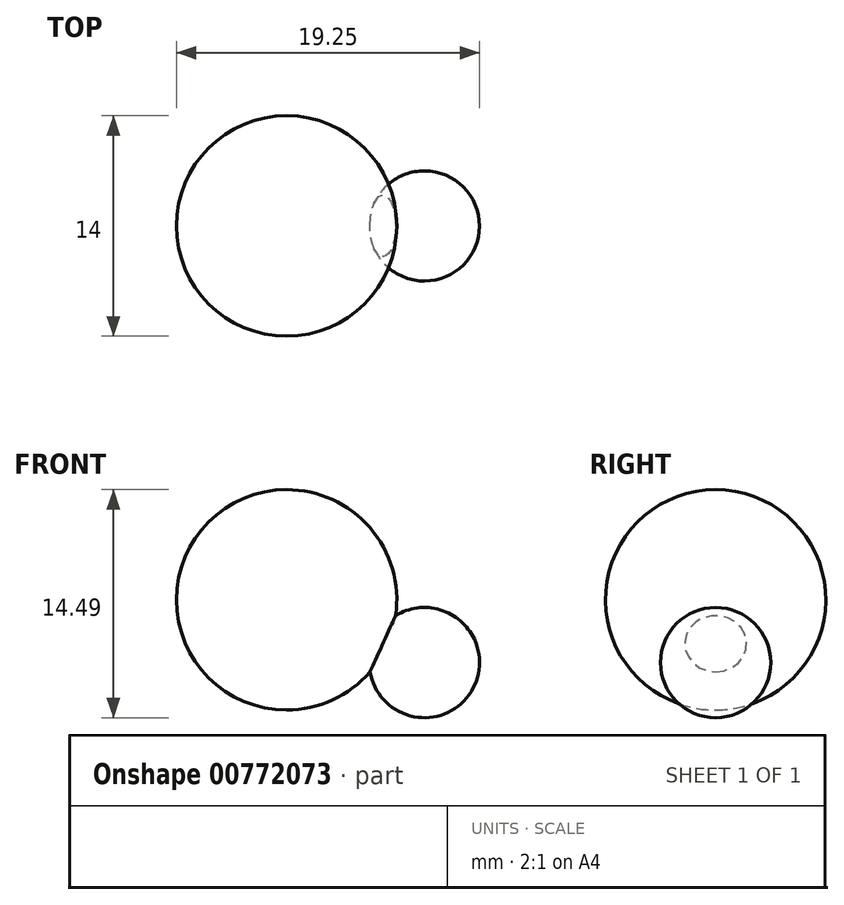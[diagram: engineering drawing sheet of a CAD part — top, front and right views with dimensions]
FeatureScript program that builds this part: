
annotation { "Feature Type Name" : "Feature", "Feature Type Description" : "" }
export const myFeature = defineFeature(function(context is Context, id is Id, definition is map)
    precondition{}
    {
        {
            var Q0;
            Q0=qCreatedBy(makeId("Front.planeOp"),FACE);
            var sketch = newSketch(context, id + "F0", { "sketchPlane" : qUnion([Q0])});
            skLineSegment(sketch, "E0", {"start": v(0, 0) * mm, "end": v(0, 14) * mm});
            skArc(sketch, "E1", {"start": v(0, 0) * mm, "mid": v(7, 7) * mm, "end": v(0, 14) * mm});
            skSolve(sketch);
        }
        {
            var Q0;
            Q0=qCreatedBy(makeId("Front.planeOp"),FACE);
            var sketch = newSketch(context, id + "F1", { "sketchPlane" : qUnion([Q0])});
            skLineSegment(sketch, "E2", {"start": v(0, 0) * mm, "end": v(0, 13.87) * mm, "construction": true});
            skLineSegment(sketch, "E3", {"start": v(0, 6.93) * mm, "end": v(6.62, 9.21) * mm, "construction": true});
            skSolve(sketch);
        }
        {
            var Q0;
            Q0=sQuery(id+"F1.wireOp",VERTEX,"E3.end");
            var Q1;
            Q1=sQuery(id+"F1.wireOp",EDGE,"E3");
            cPlane(context, id + "F2", {"entities" : qUnion([Q0, Q1]), "cplaneType" : CPlaneType.LINE_POINT, "offset" : 25.4 * mm, "width" : 152.4 * mm, "height" : 152.4 * mm});
        }
        {
            var Q0;
            Q0=makeQuery(id+"F0.imprint","IMPRINT",FACE,{"disambiguationData":[TD([[makeQuery(id+"F0.imprint","IMPRINT",EDGE,{"derivedFrom":sQuery(id+"F0.wireOp",EDGE,"E0")}),-1.0]])]});
            var Q1;
            Q1=sQuery(id+"F0.wireOp",EDGE,"E0");
            revolve(context, id + "F3", {"surfaceOperationType" : NewSurfaceOperationType.NEW, "entities" : qUnion([Q0]), "axis" : qUnion([Q1]), "revolveType" : RevolveType.FULL});
        }
        {
            var Q0;
            Q0=qCreatedBy(id+"F2.planeOp",FACE);
            var sketch = newSketch(context, id + "F4", { "sketchPlane" : qUnion([Q0])});
            skLineSegment(sketch, "E4", {"start": v(3.5, 0) * mm, "end": v(-3.5, 0) * mm});
            skArc(sketch, "E5", {"start": v(-3.5, 0) * mm, "mid": v(0, -3.5) * mm, "end": v(3.5, 0) * mm});
            skSolve(sketch);
        }
        {
            var Q0;
            Q0=makeQuery(id+"F4.imprint","IMPRINT",FACE,{"disambiguationData":[TD([[makeQuery(id+"F4.imprint","IMPRINT",EDGE,{"derivedFrom":sQuery(id+"F4.wireOp",EDGE,"E4")}),1.0]])]});
            var Q1;
            Q1=sQuery(id+"F4.wireOp",EDGE,"E4");
            revolve(context, id + "F5", {"operationType" : NewBodyOperationType.ADD, "surfaceOperationType" : NewSurfaceOperationType.NEW, "entities" : qUnion([Q0]), "axis" : qUnion([Q1]), "revolveType" : RevolveType.FULL});
        }
    });
